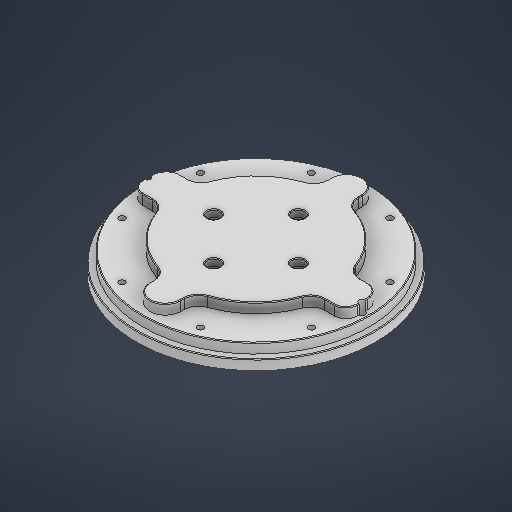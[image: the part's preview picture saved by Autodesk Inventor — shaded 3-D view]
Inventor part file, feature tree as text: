
AUTODESK INVENTOR PART (.ipt)
format: ipt  version: 2025 (Build 290162000, 162)  size: 451,584 bytes
history: native  units: mm
features: sketch x7, extrude x3, hole x3, pattern_circular x2, imported_body x1, mirror x1, chamfer x1, fillet x1
ambient origin geometry x8: Origin, YZ Plane, XZ Plane, XY Plane, X Axis, Y Axis, Z Axis, Center Point
bodies: Solid1 (feature_tree)
feature tree (19):
  imported_body  "Base"
  extrude  "Clover"  Depth=84.5mm
  hole  "Plunger Mount Holes"  [1 undecoded]
  pattern_circular  "Circular Pattern1"  Count=11  [1 undecoded]
  hole  "Seal Ring Holes"  [1 undecoded]
  pattern_circular  "Circular Pattern2"  [2 undecoded]
  hole  "Plate Mounting Holes"  [1 undecoded]
  mirror  "Mirror1"
  extrude  "Key Shape"  Depth=4.0mm
  extrude  "Bolt Recess"  Depth=10.0mm
  chamfer  "Chamfer1"  Distance=21.8mm
  fillet  "Fillet1"  Radius=10.0mm
  sketch  "Sketch1"  dims[d1=80.0mm d2=84.5mm]
  sketch  "Sketch2"  dims[d3=7.0mm d4=7.0mm]
  sketch  "Sketch3"  dims[d5=0.5mm]
  sketch  "Sketch4"  dims[d6=0.5mm]
  sketch  "Sketch5"  dims[d7=0.5mm]
  sketch  "Sketch6"  dims[d8=0.5mm]
  sketch  "Sketch7"  dims[d9=90.0deg d10=110.0mm d14=90.0deg d15=8.0mm d16=25.0mm d17=76.0mm d19=10.0mm d20=21.8mm d22=64.1mm d23=10.0mm d24=7.0mm d25=0.0mm d26=5.5mm d27=6.0mm d28=9.0mm d29=5.0mm d30=90.0deg d31=8.0mm d32=20.594885mm d33=59.9mm d35=40.0mm d36=360.0deg d38=4.4mm d39=6.0mm d40=9.0mm d41=7.2mm d42=90.0deg d43=8.0mm d44=20.594885mm d45=145.0mm d46=22.5deg d47=80.0mm d48=360.0deg d50=4.4mm d51=6.0mm d52=4.0mm d53=2.0mm d54=90.0deg d55=8.0mm d56=20.594885mm d57=81.0mm d58=35.0mm d59=1.5mm d60=0.0mm d61=20.0mm d62=6.0mm d63=0.0mm d64=0.5mm d65=2.0mm d66=45.0deg d67=4.0mm d68=10.9mm]
note: 6 required parameter values undecoded (feature->parameter linkage not recoverable at this tier; creation-order binding heuristic only, values carry confidence <= 0.55)
